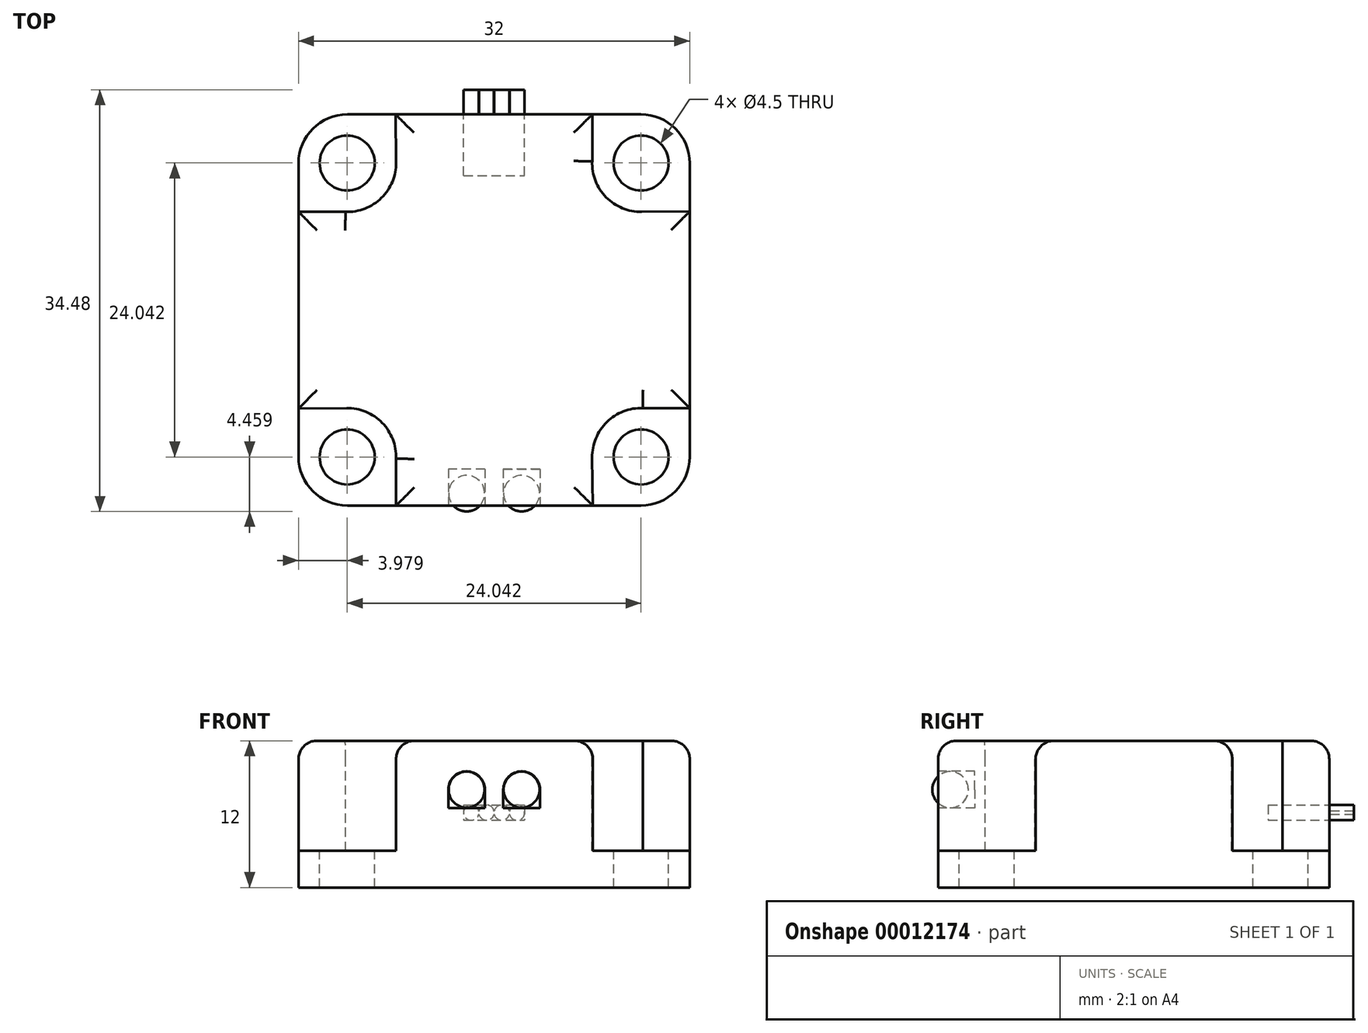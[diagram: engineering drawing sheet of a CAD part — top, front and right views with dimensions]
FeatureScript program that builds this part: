
annotation { "Feature Type Name" : "Feature", "Feature Type Description" : "" }
export const myFeature = defineFeature(function(context is Context, id is Id, definition is map)
    precondition{}
    {
        {
            var Q0;
            Q0=qCreatedBy(makeId("Top.planeOp"),FACE);
            var sketch = newSketch(context, id + "F0", { "sketchPlane" : qUnion([Q0])});
            skLineSegment(sketch, "E0.rect.bottom", {"start": v(16, 16) * mm, "end": v(-16, 16) * mm});
            skLineSegment(sketch, "E0.rect.top", {"start": v(16, -16) * mm, "end": v(-16, -16) * mm});
            skLineSegment(sketch, "E0.rect.left", {"start": v(16, 16) * mm, "end": v(16, -16) * mm});
            skLineSegment(sketch, "E0.rect.right", {"start": v(-16, 16) * mm, "end": v(-16, -16) * mm});
            skPoint(sketch, "E0.rect.middle", {"position": v(0, 0) * mm});
            skSolve(sketch);
        }
        {
            var Q0;
            Q0 = qSketchRegion(id + "F0", true);
            extrude(context, id + "F1", {"entities" : qUnion([Q0]), "depth" : 12 * mm});
        }
        {
            var Q0;
            Q0=makeQuery(id+"F1.opExtrude","CAP_FACE",FACE,{"disambiguationData":[OSD([sQuery(id+"F0.wireOp",EDGE,"E0.rect.bottom"),sQuery(id+"F0.wireOp",EDGE,"E0.rect.top"),sQuery(id+"F0.wireOp",EDGE,"E0.rect.left"),sQuery(id+"F0.wireOp",EDGE,"E0.rect.right")])],"isStart":false});
            var sketch = newSketch(context, id + "F2", { "sketchPlane" : qUnion([Q0])});
            skCircle(sketch, "E1", {"center": v(0, 0) * mm, "radius": 17 * mm, "construction": true});
            skLineSegment(sketch, "E2", {"start": v(-16, 16) * mm, "end": v(0, 0) * mm, "construction": true});
            skArc(sketch, "E3", {"start": v(-12.16, 8.02) * mm, "mid": v(-9.22, 9.16) * mm, "end": v(-8.02, 12.07) * mm});
            skLineSegment(sketch, "E4", {"start": v(-8.02, 12.07) * mm, "end": v(-8.07, 16) * mm});
            skLineSegment(sketch, "E5", {"start": v(-8.07, 16) * mm, "end": v(-16, 16) * mm});
            skLineSegment(sketch, "E6", {"start": v(-12.16, 8.02) * mm, "end": v(-16, 8.02) * mm});
            skLineSegment(sketch, "E7", {"start": v(-16, 8.02) * mm, "end": v(-16, 16) * mm});
            skLineSegment(sketch, "E8.1.0", {"start": v(-8.02, -16) * mm, "end": v(-16, -16) * mm});
            skLineSegment(sketch, "E8.1.1", {"start": v(-8.02, -12.16) * mm, "end": v(-8.02, -16) * mm});
            skArc(sketch, "E8.1.2", {"start": v(-8.02, -12.16) * mm, "mid": v(-9.16, -9.22) * mm, "end": v(-12.07, -8.02) * mm});
            skLineSegment(sketch, "E8.1.3", {"start": v(-16, -8.07) * mm, "end": v(-16, -16) * mm});
            skLineSegment(sketch, "E8.1.4", {"start": v(-12.07, -8.02) * mm, "end": v(-16, -8.07) * mm});
            skLineSegment(sketch, "E8.2.0", {"start": v(16, -8.02) * mm, "end": v(16, -16) * mm});
            skLineSegment(sketch, "E8.2.1", {"start": v(12.16, -8.02) * mm, "end": v(16, -8.02) * mm});
            skArc(sketch, "E8.2.2", {"start": v(12.16, -8.02) * mm, "mid": v(9.22, -9.16) * mm, "end": v(8.02, -12.07) * mm});
            skLineSegment(sketch, "E8.2.3", {"start": v(8.07, -16) * mm, "end": v(16, -16) * mm});
            skLineSegment(sketch, "E8.2.4", {"start": v(8.02, -12.07) * mm, "end": v(8.07, -16) * mm});
            skLineSegment(sketch, "E8.3.0", {"start": v(8.02, 16) * mm, "end": v(16, 16) * mm});
            skLineSegment(sketch, "E8.3.1", {"start": v(8.02, 12.16) * mm, "end": v(8.02, 16) * mm});
            skArc(sketch, "E8.3.2", {"start": v(8.02, 12.16) * mm, "mid": v(9.16, 9.22) * mm, "end": v(12.07, 8.02) * mm});
            skLineSegment(sketch, "E8.3.3", {"start": v(16, 8.07) * mm, "end": v(16, 16) * mm});
            skLineSegment(sketch, "E8.3.4", {"start": v(12.07, 8.02) * mm, "end": v(16, 8.07) * mm});
            skSolve(sketch);
        }
        {
            var Q0;
            Q0 = qSketchRegion(id + "F2", true);
            extrude(context, id + "F3", {"entities" : qUnion([Q0]), "operationType" : NewBodyOperationType.REMOVE, "oppositeDirection" : true, "depth" : 9 * mm});
        }
        {
            var Q0;
            Q0=makeQuery(id+"F1.opExtrude","SWEPT_EDGE",EDGE,{"disambiguationData":[OSD([sQuery(id+"F0.wireOp",EDGE,"E0.rect.bottom"),sQuery(id+"F0.wireOp",EDGE,"E0.rect.right")])]});
            var Q1;
            Q1=makeQuery(id+"F1.opExtrude","SWEPT_EDGE",EDGE,{"disambiguationData":[OSD([sQuery(id+"F0.wireOp",EDGE,"E0.rect.bottom"),sQuery(id+"F0.wireOp",EDGE,"E0.rect.left")])]});
            var Q2;
            Q2=makeQuery(id+"F1.opExtrude","SWEPT_EDGE",EDGE,{"disambiguationData":[OSD([sQuery(id+"F0.wireOp",EDGE,"E0.rect.top"),sQuery(id+"F0.wireOp",EDGE,"E0.rect.left")])]});
            var Q3;
            Q3=makeQuery(id+"F1.opExtrude","SWEPT_EDGE",EDGE,{"disambiguationData":[OSD([sQuery(id+"F0.wireOp",EDGE,"E0.rect.top"),sQuery(id+"F0.wireOp",EDGE,"E0.rect.right")])]});
            fillet(context, id + "F4", {"entities" : qUnion([Q0, Q1, Q2, Q3]), "radius" : 4 * mm, "tangentPropagation" : true, "allowEdgeOverflow" : false});
        }
        {
            var Q0;
            Q0=makeQuery(id+"F1.opExtrude","CAP_FACE",FACE,{"disambiguationData":[OSD([sQuery(id+"F0.wireOp",EDGE,"E0.rect.bottom"),sQuery(id+"F0.wireOp",EDGE,"E0.rect.top"),sQuery(id+"F0.wireOp",EDGE,"E0.rect.left"),sQuery(id+"F0.wireOp",EDGE,"E0.rect.right")])],"isStart":false});
            var Q1;
            Q1=makeQuery(id+"F3.boolean.opBoolean","COPY",EDGE,{"derivedFrom":makeQuery(id+"F3.opExtrude","SWEPT_EDGE",EDGE,{"disambiguationData":[OSD([sQuery(id+"F0.wireOp",EDGE,"E0.rect.top"),sQuery(id+"F2.wireOp",EDGE,"E8.2.3"),sQuery(id+"F2.wireOp",EDGE,"E8.2.4")])]})});
            var Q2;
            Q2=makeQuery(id+"F3.boolean.opBoolean","COPY",EDGE,{"derivedFrom":makeQuery(id+"F3.opExtrude","SWEPT_EDGE",EDGE,{"disambiguationData":[OSD([sQuery(id+"F0.wireOp",EDGE,"E0.rect.left"),sQuery(id+"F2.wireOp",EDGE,"E8.2.0"),sQuery(id+"F2.wireOp",EDGE,"E8.2.1")])]})});
            var Q3;
            Q3=makeQuery(id+"F3.boolean.opBoolean","COPY",EDGE,{"derivedFrom":makeQuery(id+"F3.opExtrude","SWEPT_EDGE",EDGE,{"disambiguationData":[OSD([sQuery(id+"F0.wireOp",EDGE,"E0.rect.left"),sQuery(id+"F2.wireOp",EDGE,"E8.3.3"),sQuery(id+"F2.wireOp",EDGE,"E8.3.4")])]})});
            var Q4;
            Q4=makeQuery(id+"F3.boolean.opBoolean","COPY",EDGE,{"derivedFrom":makeQuery(id+"F3.opExtrude","SWEPT_EDGE",EDGE,{"disambiguationData":[OSD([sQuery(id+"F0.wireOp",EDGE,"E0.rect.top"),sQuery(id+"F2.wireOp",EDGE,"E8.1.0"),sQuery(id+"F2.wireOp",EDGE,"E8.1.1")])]})});
            var Q5;
            Q5=makeQuery(id+"F3.boolean.opBoolean","COPY",EDGE,{"derivedFrom":makeQuery(id+"F3.opExtrude","SWEPT_EDGE",EDGE,{"disambiguationData":[OSD([sQuery(id+"F0.wireOp",EDGE,"E0.rect.right"),sQuery(id+"F2.wireOp",EDGE,"E8.1.3"),sQuery(id+"F2.wireOp",EDGE,"E8.1.4")])]})});
            var Q6;
            Q6=makeQuery(id+"F3.boolean.opBoolean","COPY",EDGE,{"derivedFrom":makeQuery(id+"F3.opExtrude","SWEPT_EDGE",EDGE,{"disambiguationData":[OSD([sQuery(id+"F0.wireOp",EDGE,"E0.rect.bottom"),sQuery(id+"F2.wireOp",EDGE,"E8.3.0"),sQuery(id+"F2.wireOp",EDGE,"E8.3.1")])]})});
            var Q7;
            Q7=makeQuery(id+"F3.boolean.opBoolean","COPY",EDGE,{"derivedFrom":makeQuery(id+"F3.opExtrude","SWEPT_EDGE",EDGE,{"disambiguationData":[OSD([sQuery(id+"F0.wireOp",EDGE,"E0.rect.bottom"),sQuery(id+"F2.wireOp",EDGE,"E4"),sQuery(id+"F2.wireOp",EDGE,"E5")])]})});
            var Q8;
            Q8=makeQuery(id+"F3.boolean.opBoolean","COPY",EDGE,{"derivedFrom":makeQuery(id+"F3.opExtrude","SWEPT_EDGE",EDGE,{"disambiguationData":[OSD([sQuery(id+"F0.wireOp",EDGE,"E0.rect.right"),sQuery(id+"F2.wireOp",EDGE,"E6"),sQuery(id+"F2.wireOp",EDGE,"E7")])]})});
            fillet(context, id + "F5", {"entities" : qUnion([Q0, Q1, Q2, Q3, Q4, Q5, Q6, Q7, Q8]), "radius" : 1.5 * mm, "tangentPropagation" : true, "allowEdgeOverflow" : false});
        }
        {
            var Q0;
            Q0=makeQuery(id+"F1.opExtrude","SWEPT_FACE",FACE,{"disambiguationData":[OSD([sQuery(id+"F0.wireOp",EDGE,"E0.rect.top")])]});
            var sketch = newSketch(context, id + "F6", { "sketchPlane" : qUnion([Q0])});
            skLineSegment(sketch, "E9", {"start": v(0, 0) * mm, "end": v(0, 16) * mm, "construction": true});
            skLineSegment(sketch, "E10", {"start": v(0, 8) * mm, "end": v(2.25, 8) * mm, "construction": true});
            skArc(sketch, "E11", {"start": v(3.75, 8) * mm, "mid": v(2.25, 9.5) * mm, "end": v(0.75, 8) * mm});
            skLineSegment(sketch, "E12.top", {"start": v(0.75, 6.5) * mm, "end": v(3.75, 6.5) * mm});
            skLineSegment(sketch, "E12.left", {"start": v(0.75, 8) * mm, "end": v(0.75, 6.5) * mm});
            skLineSegment(sketch, "E12.right", {"start": v(3.75, 8) * mm, "end": v(3.75, 6.5) * mm});
            skLineSegment(sketch, "E13.0.MirrorCS", {"start": v(-0.75, 6.5) * mm, "end": v(-3.75, 6.5) * mm});
            skLineSegment(sketch, "E13.1.MirrorCS", {"start": v(-0.75, 8) * mm, "end": v(-0.75, 6.5) * mm});
            skLineSegment(sketch, "E13.2.MirrorCS", {"start": v(-3.75, 8) * mm, "end": v(-3.75, 6.5) * mm});
            skArc(sketch, "E13.3.MirrorCS", {"start": v(-3.75, 8) * mm, "mid": v(-2.25, 9.5) * mm, "end": v(-0.75, 8) * mm});
            skSolve(sketch);
        }
        {
            var Q0;
            Q0 = qSketchRegion(id + "F6", true);
            extrude(context, id + "F7", {"entities" : qUnion([Q0]), "operationType" : NewBodyOperationType.REMOVE, "oppositeDirection" : true, "depth" : 3 * mm});
        }
        {
            var Q0;
            Q0=makeQuery(id+"F1.opExtrude","SWEPT_FACE",FACE,{"disambiguationData":[OSD([sQuery(id+"F0.wireOp",EDGE,"E0.rect.bottom")])]});
            var sketch = newSketch(context, id + "F8", { "sketchPlane" : qUnion([Q0])});
            skLineSegment(sketch, "E14.rect.bottom", {"start": v(2.5, 6.75) * mm, "end": v(-2.5, 6.75) * mm});
            skLineSegment(sketch, "E14.rect.top", {"start": v(2.5, 5.5) * mm, "end": v(-2.5, 5.5) * mm});
            skLineSegment(sketch, "E14.rect.left", {"start": v(2.5, 6.75) * mm, "end": v(2.5, 5.5) * mm});
            skLineSegment(sketch, "E14.rect.right", {"start": v(-2.5, 6.75) * mm, "end": v(-2.5, 5.5) * mm});
            skPoint(sketch, "E14.rect.middle", {"position": v(0, 6.12) * mm});
            skSolve(sketch);
        }
        {
            var Q0;
            Q0 = qSketchRegion(id + "F8", true);
            extrude(context, id + "F9", {"entities" : qUnion([Q0]), "operationType" : NewBodyOperationType.REMOVE, "oppositeDirection" : true, "depth" : 5 * mm});
        }
        {
            var Q0;
            Q0=makeQuery(id+"F1.opExtrude","SWEPT_FACE",FACE,{"disambiguationData":[OSD([sQuery(id+"F0.wireOp",EDGE,"E0.rect.bottom")])]});
            var sketch = newSketch(context, id + "F10", { "sketchPlane" : qUnion([Q0])});
            skArc(sketch, "E15", {"start": v(1.27, 5.97) * mm, "mid": v(2.5, 6.14) * mm, "end": v(1.26, 6.25) * mm});
            skLineSegment(sketch, "E16", {"start": v(2.5, 6.12) * mm, "end": v(-2.5, 6.12) * mm, "construction": true});
            skArc(sketch, "E17.1.0.0", {"start": v(0.02, 5.97) * mm, "mid": v(0.63, 5.5) * mm, "end": v(1.23, 5.97) * mm});
            skArc(sketch, "E17.2.0.0", {"start": v(-1.23, 5.97) * mm, "mid": v(-0.62, 5.5) * mm, "end": v(-0.02, 5.97) * mm});
            skArc(sketch, "E17.3.0.0", {"start": v(-1.26, 6.25) * mm, "mid": v(-2.5, 6.14) * mm, "end": v(-1.27, 5.97) * mm});
            skLineSegment(sketch, "E17.direction1", {"start": v(1.88, 6.12) * mm, "end": v(0.63, 6.12) * mm, "construction": true});
            skLineSegment(sketch, "E18.rect.bottom", {"start": v(-1.26, 6.25) * mm, "end": v(-1.24, 6.25) * mm});
            skLineSegment(sketch, "E18.rect.top", {"start": v(-1.27, 5.97) * mm, "end": v(-1.23, 5.97) * mm});
            skPoint(sketch, "E18.rect.middle", {"position": v(0, 6.13) * mm});
            skLineSegment(sketch, "E19.trimOffspring", {"start": v(-0.01, 6.25) * mm, "end": v(0.01, 6.25) * mm});
            skArc(sketch, "E20.trimOffspring", {"start": v(-0.01, 6.25) * mm, "mid": v(-0.62, 6.75) * mm, "end": v(-1.24, 6.25) * mm});
            skLineSegment(sketch, "E21.trimOffspring", {"start": v(1.24, 6.25) * mm, "end": v(1.26, 6.25) * mm});
            skLineSegment(sketch, "E22.trimOffspring", {"start": v(1.23, 5.97) * mm, "end": v(1.27, 5.97) * mm});
            skArc(sketch, "E23.trimOffspring", {"start": v(1.24, 6.25) * mm, "mid": v(0.63, 6.75) * mm, "end": v(0.01, 6.25) * mm});
            skLineSegment(sketch, "E24", {"start": v(-0.02, 5.97) * mm, "end": v(0.02, 5.97) * mm});
            skSolve(sketch);
        }
        {
            var Q0;
            Q0 = qSketchRegion(id + "F10", true);
            extrude(context, id + "F11", {"entities" : qUnion([Q0]), "operationType" : NewBodyOperationType.ADD, "depth" : 2 * mm});
        }
        {
            var Q0;
            Q0=makeQuery(id+"F1.opExtrude","SWEPT_FACE",FACE,{"disambiguationData":[OSD([sQuery(id+"F0.wireOp",EDGE,"E0.rect.top")])]});
            cPlane(context, id + "F12", {"entities" : qUnion([Q0]), "cplaneType" : CPlaneType.OFFSET, "offset" : 1 * mm, "oppositeDirection" : true, "width" : 152.4 * mm, "height" : 152.4 * mm});
        }
        {
            var Q0;
            Q0=qCreatedBy(id+"F12.planeOp",FACE);
            var sketch = newSketch(context, id + "F13", { "sketchPlane" : qUnion([Q0])});
            skArc(sketch, "E25", {"start": v(0.77, 8) * mm, "mid": v(2.25, 6.52) * mm, "end": v(3.72, 8) * mm});
            skLineSegment(sketch, "E26", {"start": v(2.25, 8) * mm, "end": v(-2.18, 8) * mm, "construction": true});
            skLineSegment(sketch, "E27", {"start": v(0, 8) * mm, "end": v(0, 9.48) * mm, "construction": true});
            skArc(sketch, "E28.0.MirrorC", {"start": v(-0.77, 8) * mm, "mid": v(-2.25, 6.52) * mm, "end": v(-3.72, 8) * mm});
            skLineSegment(sketch, "E29", {"start": v(3.72, 8) * mm, "end": v(0.77, 8) * mm});
            skLineSegment(sketch, "E30.trimOffspring", {"start": v(-0.77, 8) * mm, "end": v(-3.72, 8) * mm});
            skSolve(sketch);
        }
        {
            var Q0;
            Q0 = qSketchRegion(id + "F13", true);
            var Q1;
            Q1=sQuery(id+"F13.wireOp",EDGE,"E26");
            revolve(context, id + "F14", {"operationType" : NewBodyOperationType.ADD, "entities" : qUnion([Q0]), "axis" : qUnion([Q1]), "revolveType" : RevolveType.FULL});
        }
        {
            var Q0;
            Q0=makeQuery(id+"F3.boolean.opBoolean","COPY",FACE,{"derivedFrom":makeQuery(id+"F3.opExtrude","CAP_FACE",FACE,{"disambiguationData":[OSD([sQuery(id+"F2.wireOp",EDGE,"E8.3.0"),sQuery(id+"F2.wireOp",EDGE,"E8.3.1"),sQuery(id+"F2.wireOp",EDGE,"E8.3.2"),sQuery(id+"F2.wireOp",EDGE,"E8.3.3"),sQuery(id+"F2.wireOp",EDGE,"E8.3.4")])],"isStart":false})});
            var sketch = newSketch(context, id + "F15", { "sketchPlane" : qUnion([Q0])});
            skCircle(sketch, "E31", {"center": v(0, 0) * mm, "radius": 17 * mm, "construction": true});
            skLineSegment(sketch, "E32", {"start": v(0, 0) * mm, "end": v(14.83, 14.83) * mm, "construction": true});
            skCircle(sketch, "E33", {"center": v(12.02, 12.02) * mm, "radius": 2.25 * mm});
            skCircle(sketch, "E34.1.0", {"center": v(-12.02, 12.02) * mm, "radius": 2.25 * mm});
            skCircle(sketch, "E34.2.0", {"center": v(-12.02, -12.02) * mm, "radius": 2.25 * mm});
            skCircle(sketch, "E34.3.0", {"center": v(12.02, -12.02) * mm, "radius": 2.25 * mm});
            skSolve(sketch);
        }
        {
            var Q0;
            Q0 = qSketchRegion(id + "F15", true);
            extrude(context, id + "F16", {"entities" : qUnion([Q0]), "operationType" : NewBodyOperationType.REMOVE, "endBound" : BoundingType.THROUGH_ALL, "oppositeDirection" : true, "depth" : 25.4 * mm});
        }
    });
